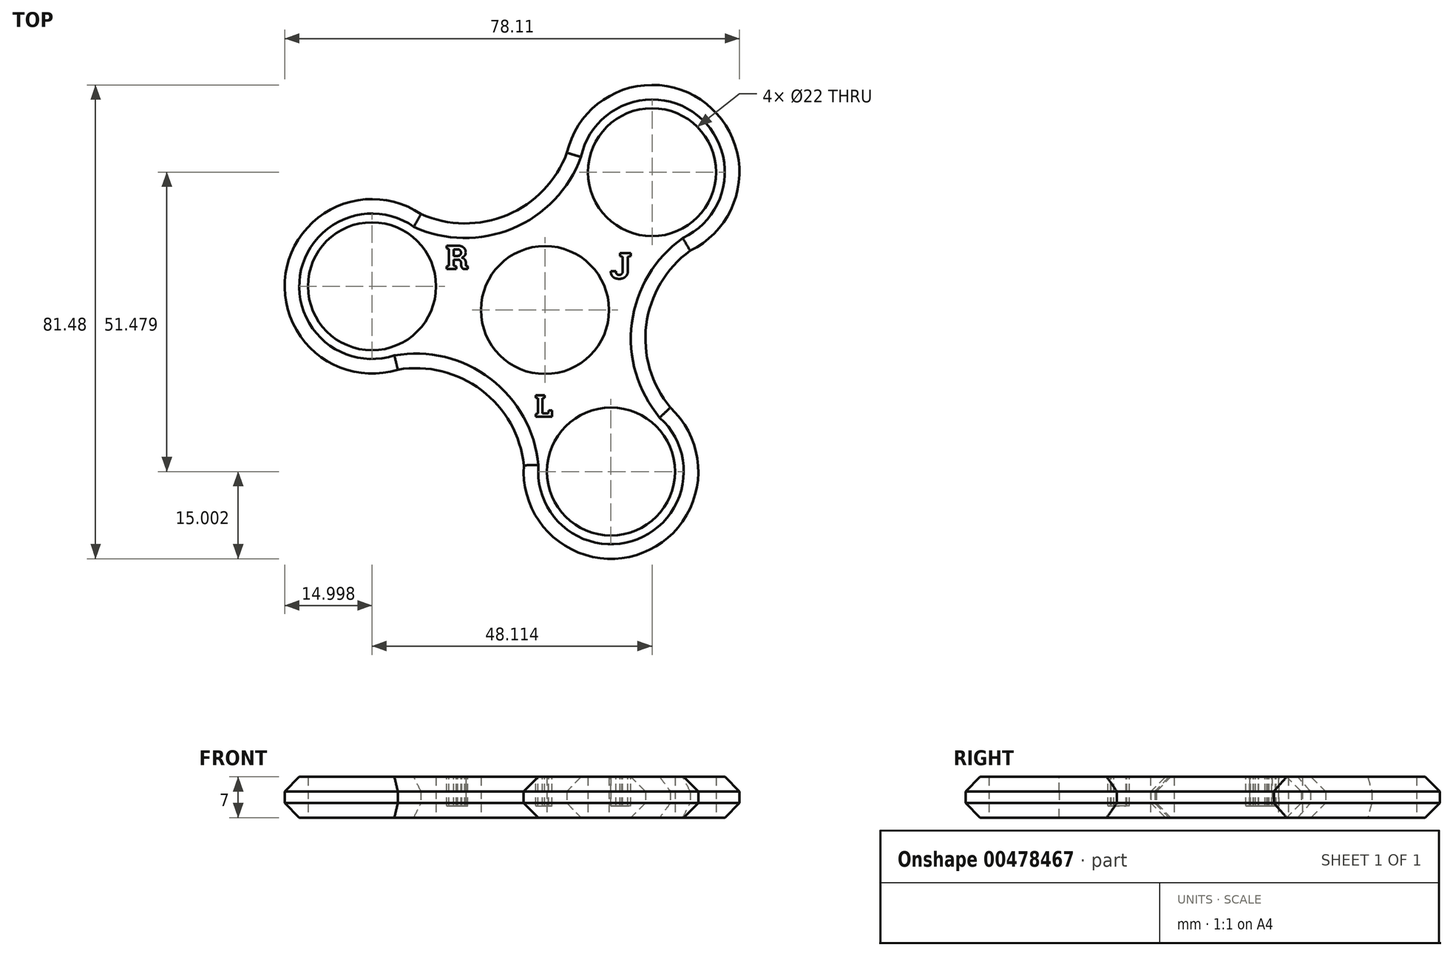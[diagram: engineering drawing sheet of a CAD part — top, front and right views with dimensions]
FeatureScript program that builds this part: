
annotation { "Feature Type Name" : "Feature", "Feature Type Description" : "" }
export const myFeature = defineFeature(function(context is Context, id is Id, definition is map)
    precondition{}
    {
        {
            var Q0;
            Q0=qCreatedBy(makeId("Top.planeOp"),FACE);
            var sketch = newSketch(context, id + "F0", { "sketchPlane" : qUnion([Q0])});
            skCircle(sketch, "E0", {"center": v(0, 0) * mm, "radius": 11 * mm});
            skCircle(sketch, "E1", {"center": v(0, 0) * mm, "radius": 15 * mm});
            skCircle(sketch, "E2", {"center": v(18.4, 23.7) * mm, "radius": 11 * mm});
            skCircle(sketch, "E3.1.0", {"center": v(-29.72, 4.08) * mm, "radius": 11 * mm});
            skCircle(sketch, "E3.2.0", {"center": v(11.33, -27.78) * mm, "radius": 11 * mm});
            skCircle(sketch, "E4", {"center": v(-29.72, 4.08) * mm, "radius": 15 * mm});
            skCircle(sketch, "E5.1.0", {"center": v(11.33, -27.78) * mm, "radius": 15 * mm});
            skCircle(sketch, "E5.2.0", {"center": v(18.4, 23.7) * mm, "radius": 15 * mm});
            skArc(sketch, "E6", {"start": v(-21.3, 16.5) * mm, "mid": v(-6.5, 16.34) * mm, "end": v(3.77, 27.03) * mm});
            skArc(sketch, "E7.1.0", {"start": v(-3.63, -26.7) * mm, "mid": v(-10.9, -13.8) * mm, "end": v(-25.3, -10.25) * mm});
            skArc(sketch, "E7.2.0", {"start": v(24.94, 10.2) * mm, "mid": v(17.4, -2.55) * mm, "end": v(21.52, -16.78) * mm});
            skSolve(sketch);
        }
        {
            var Q0;
            {var subQ5=sQuery(id+"F0.wireOp",EDGE,"E6");Q0=makeQuery(id+"F0.imprint","IMPRINT",FACE,{"disambiguationData":[TD([[makeQuery(id+"F0.imprint","IMPRINT",EDGE,{"derivedFrom":subQ5}),-1.0]])]});}
            var Q1;
            {var subQ5=sQuery(id+"F0.wireOp",EDGE,"E7.1.0");Q1=makeQuery(id+"F0.imprint","IMPRINT",FACE,{"disambiguationData":[TD([[makeQuery(id+"F0.imprint","IMPRINT",EDGE,{"derivedFrom":subQ5}),-1.0]])]});}
            var Q2;
            {var subQ5=sQuery(id+"F0.wireOp",EDGE,"E7.2.0");Q2=makeQuery(id+"F0.imprint","IMPRINT",FACE,{"disambiguationData":[TD([[makeQuery(id+"F0.imprint","IMPRINT",EDGE,{"derivedFrom":subQ5}),-1.0]])]});}
            var Q3;
            Q3=makeQuery(id+"F0.imprint","IMPRINT",FACE,{"disambiguationData":[TD([[makeQuery(id+"F0.imprint","IMPRINT",EDGE,{"derivedFrom":sQuery(id+"F0.wireOp",EDGE,"E0")}),-1.0]])]});
            var Q4;
            Q4=makeQuery(id+"F0.imprint","IMPRINT",FACE,{"disambiguationData":[TD([[makeQuery(id+"F0.imprint","IMPRINT",EDGE,{"derivedFrom":sQuery(id+"F0.wireOp",EDGE,"E3.1.0")}),-1.0]])]});
            var Q5;
            Q5=makeQuery(id+"F0.imprint","IMPRINT",FACE,{"disambiguationData":[TD([[makeQuery(id+"F0.imprint","IMPRINT",EDGE,{"derivedFrom":sQuery(id+"F0.wireOp",EDGE,"E2")}),-1.0]])]});
            var Q6;
            Q6 = qSketchRegion(id + "F0", true);
            var Q7;
            Q7=makeQuery(id+"F0.imprint","IMPRINT",FACE,{"disambiguationData":[TD([[makeQuery(id+"F0.imprint","IMPRINT",EDGE,{"derivedFrom":sQuery(id+"F0.wireOp",EDGE,"E3.2.0")}),-1.0]])]});
            extrude(context, id + "F1", {"entities" : qUnion([Q0, Q1, Q2, Q3, Q4, Q5, Q6, Q7]), "depth" : 7 * mm});
        }
        {
            var Q0;
            Q0=makeQuery(id+"F1.opExtrude","CAP_EDGE",EDGE,{"disambiguationData":[OSD([sQuery(id+"F0.wireOp",EDGE,"E7.1.0")])],"isStart":false});
            var Q1;
            Q1=makeQuery(id+"F1.opExtrude","CAP_EDGE",EDGE,{"disambiguationData":[OSD([sQuery(id+"F0.wireOp",EDGE,"E7.1.0")])],"isStart":true});
            var Q2;
            Q2=makeQuery(id+"F1.opExtrude","CAP_EDGE",EDGE,{"disambiguationData":[OSD([sQuery(id+"F0.wireOp",EDGE,"E6")])],"isStart":false});
            var Q3;
            Q3=makeQuery(id+"F1.opExtrude","CAP_EDGE",EDGE,{"disambiguationData":[OSD([sQuery(id+"F0.wireOp",EDGE,"E7.2.0")])],"isStart":false});
            var Q4;
            Q4=makeQuery(id+"F1.opExtrude","CAP_EDGE",EDGE,{"disambiguationData":[OSD([sQuery(id+"F0.wireOp",EDGE,"E7.2.0")])],"isStart":true});
            var Q5;
            Q5=makeQuery(id+"F1.opExtrude","CAP_EDGE",EDGE,{"disambiguationData":[OSD([sQuery(id+"F0.wireOp",EDGE,"E6")])],"isStart":true});
            var Q6;
            Q6=makeQuery(id+"F1.opExtrude","CAP_EDGE",EDGE,{"disambiguationData":[OSD([sQuery(id+"F0.wireOp",EDGE,"E5.2.0")])],"isStart":false});
            var Q7;
            Q7=makeQuery(id+"F1.opExtrude","CAP_EDGE",EDGE,{"disambiguationData":[OSD([sQuery(id+"F0.wireOp",EDGE,"E5.2.0")])],"isStart":true});
            var Q8;
            Q8=makeQuery(id+"F1.opExtrude","CAP_EDGE",EDGE,{"disambiguationData":[OSD([sQuery(id+"F0.wireOp",EDGE,"E5.1.0")])],"isStart":false});
            var Q9;
            Q9=makeQuery(id+"F1.opExtrude","CAP_EDGE",EDGE,{"disambiguationData":[OSD([sQuery(id+"F0.wireOp",EDGE,"E5.1.0")])],"isStart":true});
            var Q10;
            Q10=makeQuery(id+"F1.opExtrude","CAP_EDGE",EDGE,{"disambiguationData":[OSD([sQuery(id+"F0.wireOp",EDGE,"E4")])],"isStart":false});
            var Q11;
            Q11=makeQuery(id+"F1.opExtrude","CAP_EDGE",EDGE,{"disambiguationData":[OSD([sQuery(id+"F0.wireOp",EDGE,"E4")])],"isStart":true});
            chamfer(context, id + "F2", {"entities" : qUnion([Q0, Q1, Q2, Q3, Q4, Q5, Q6, Q7, Q8, Q9, Q10, Q11]), "chamferType" : ChamferType.OFFSET_ANGLE, "width" : 2.5 * mm, "oppositeDirection" : false, "angle" : 45 * degree, "tangentPropagation" : true});
        }
        {
            var Q0;
            Q0=makeQuery(id+"F1.opExtrude","CAP_FACE",FACE,{"disambiguationData":[OSD([sQuery(id+"F0.wireOp",EDGE,"E0"),sQuery(id+"F0.wireOp",EDGE,"E2"),sQuery(id+"F0.wireOp",EDGE,"E3.1.0"),sQuery(id+"F0.wireOp",EDGE,"E3.2.0"),sQuery(id+"F0.wireOp",EDGE,"E4"),sQuery(id+"F0.wireOp",EDGE,"E5.1.0"),sQuery(id+"F0.wireOp",EDGE,"E5.2.0"),sQuery(id+"F0.wireOp",EDGE,"E6"),sQuery(id+"F0.wireOp",EDGE,"E7.1.0"),sQuery(id+"F0.wireOp",EDGE,"E7.2.0")])],"isStart":false});
            var sketch = newSketch(context, id + "F3", { "sketchPlane" : qUnion([Q0])});
            skText(sketch, "E8", { "text": "J", "fontName": "RobotoSlab-Bold.ttf"});
            skText(sketch, "E9", { "text": "L", "fontName": "RobotoSlab-Bold.ttf"});
            skText(sketch, "E10", { "text": "R", "fontName": "RobotoSlab-Bold.ttf"});
            const initialGuessF3  = {"E8": [0.0112, 0.00542, 1, 0, 0.00444], "E9": [-0.00172, -0.01832, 1, 0, 0.00372], "E10": [-0.01707, 0.00703, 1, 0, 0.0041]};
            skSetInitialGuess(sketch, initialGuessF3);
            skSolve(sketch);
        }
        {
            var Q0;
            Q0=makeQuery(id+"F3.imprint","IMPRINT",FACE,{"disambiguationData":[TD([[makeQuery(id+"F3.imprint","IMPRINT",EDGE,{"derivedFrom":sQuery(id+"F3.wireOp",EDGE,"E8.sketch_text.stroke-0")}),-1.0]])]});
            var Q1;
            Q1=makeQuery(id+"F3.imprint","IMPRINT",FACE,{"disambiguationData":[TD([[makeQuery(id+"F3.imprint","IMPRINT",EDGE,{"derivedFrom":sQuery(id+"F3.wireOp",EDGE,"E10.sketch_text.stroke-0")}),-1.0]])]});
            var Q2;
            Q2=makeQuery(id+"F3.imprint","IMPRINT",FACE,{"disambiguationData":[TD([[makeQuery(id+"F3.imprint","IMPRINT",EDGE,{"derivedFrom":sQuery(id+"F3.wireOp",EDGE,"E9.sketch_text.stroke-0")}),-1.0]])]});
            extrude(context, id + "F4", {"entities" : qUnion([Q0, Q1, Q2]), "operationType" : NewBodyOperationType.REMOVE, "oppositeDirection" : true, "depth" : 5 * mm});
        }
    });
